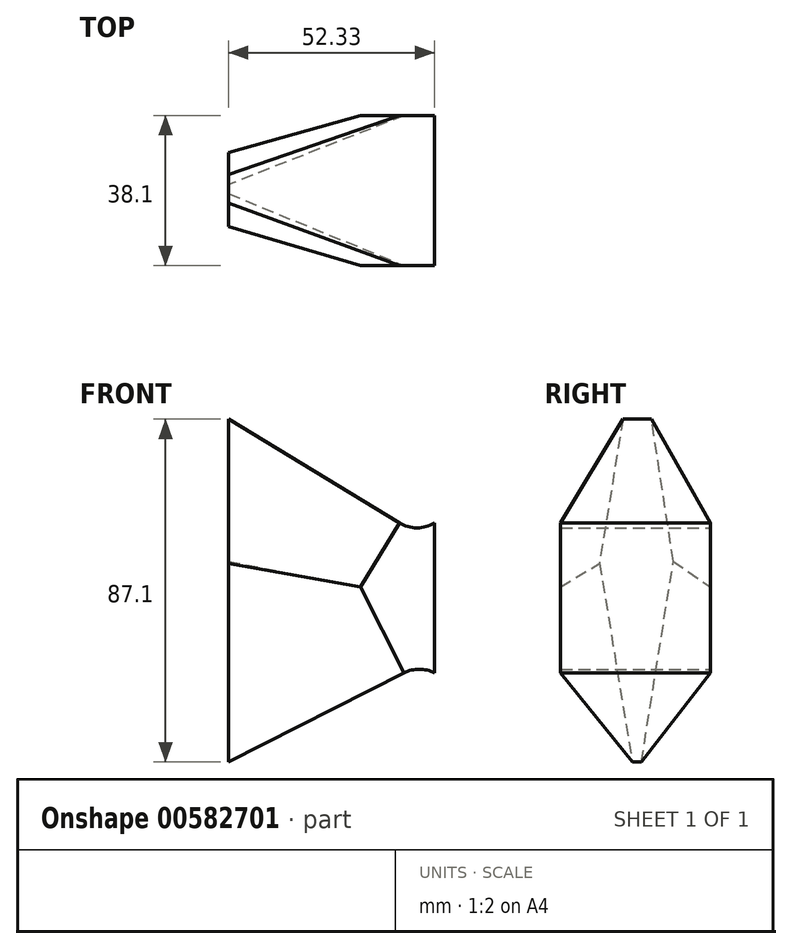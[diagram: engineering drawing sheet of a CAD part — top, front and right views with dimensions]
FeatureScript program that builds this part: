
annotation { "Feature Type Name" : "Feature", "Feature Type Description" : "" }
export const myFeature = defineFeature(function(context is Context, id is Id, definition is map)
    precondition{}
    {
        {
            var Q0;
            Q0=qCreatedBy(makeId("Front.planeOp"),FACE);
            var sketch = newSketch(context, id + "F0", { "sketchPlane" : qUnion([Q0])});
            skLineSegment(sketch, "E0", {"start": v(27.77, 20.35) * mm, "end": v(27.77, -17.75) * mm});
            skArc(sketch, "E1", {"start": v(18.86, 20.35) * mm, "mid": v(23.32, 19.1) * mm, "end": v(27.77, 20.35) * mm});
            skArc(sketch, "E2", {"start": v(27.77, -17.75) * mm, "mid": v(23.9, -16.83) * mm, "end": v(20, -17.75) * mm});
            skLineSegment(sketch, "E3", {"start": v(18.86, 20.35) * mm, "end": v(-24.56, 46.72) * mm});
            skLineSegment(sketch, "E4", {"start": v(20, -17.75) * mm, "end": v(-24.56, -40.38) * mm});
            skLineSegment(sketch, "E5", {"start": v(-24.56, -40.38) * mm, "end": v(-24.56, 46.72) * mm});
            skSolve(sketch);
        }
        {
            var Q0;
            Q0 = qSketchRegion(id + "F0", true);
            extrude(context, id + "F1", {"entities" : qUnion([Q0]), "depth" : 38.1 * mm, "offsetDistance" : 25.4 * mm});
        }
        {
            var Q0;
            Q0=makeQuery(id+"F1.opExtrude","SWEPT_FACE",FACE,{"disambiguationData":[OSD([sQuery(id+"F0.wireOp",EDGE,"E4")])]});
            var sketch = newSketch(context, id + "F2", { "sketchPlane" : qUnion([Q0])});
            skLineSegment(sketch, "E6.0", {"start": v(9.8, 0) * mm, "end": v(-40.17, 0) * mm});
            skLineSegment(sketch, "E7.0", {"start": v(-40.17, 38.1) * mm, "end": v(-40.17, 0) * mm});
            skLineSegment(sketch, "E8.0", {"start": v(9.8, 38.1) * mm, "end": v(-40.17, 38.1) * mm});
            skLineSegment(sketch, "E9", {"start": v(9.8, 0) * mm, "end": v(-40.17, 17.52) * mm});
            skLineSegment(sketch, "E10", {"start": v(-40.17, 19.86) * mm, "end": v(9.8, 38.1) * mm});
            skLineSegment(sketch, "E11.0", {"start": v(33.97, 38.1) * mm, "end": v(16.73, 38.1) * mm, "construction": true});
            skLineSegment(sketch, "E12.0", {"start": v(33.97, 38.1) * mm, "end": v(16.73, 38.1) * mm});
            skSolve(sketch);
        }
        {
            var Q0;
            {var subQ0=sQuery(id+"F2.wireOp",EDGE,"E6.0");Q0=makeQuery(id+"F2.imprint","IMPRINT",FACE,{"disambiguationData":[TD([[makeQuery(id+"F2.imprint","IMPRINT",EDGE,{"derivedFrom":subQ0}),-1.0]])]});}
            var Q1;
            {var subQ0=sQuery(id+"F2.wireOp",EDGE,"E8.0");Q1=makeQuery(id+"F2.imprint","IMPRINT",FACE,{"disambiguationData":[TD([[makeQuery(id+"F2.imprint","IMPRINT",EDGE,{"derivedFrom":subQ0}),1.0]])]});}
            extrude(context, id + "F3", {"entities" : qUnion([Q0, Q1]), "operationType" : NewBodyOperationType.REMOVE, "oppositeDirection" : true, "depth" : 101.6 * mm, "offsetDistance" : 25.4 * mm});
        }
        {
            var Q0;
            Q0=makeQuery(id+"F1.opExtrude","SWEPT_FACE",FACE,{"disambiguationData":[OSD([sQuery(id+"F0.wireOp",EDGE,"E3")])]});
            var sketch = newSketch(context, id + "F4", { "sketchPlane" : qUnion([Q0])});
            skLineSegment(sketch, "E13", {"start": v(5.55, -38.1) * mm, "end": v(-45.25, -22.26) * mm});
            skLineSegment(sketch, "E14", {"start": v(-45.25, -22.26) * mm, "end": v(-45.25, -14.97) * mm});
            skLineSegment(sketch, "E15", {"start": v(-45.25, -14.97) * mm, "end": v(5.55, 0) * mm});
            skSolve(sketch);
        }
        {
            var Q0;
            {var subQ0=sQuery(id+"F4.wireOp",EDGE,"E13");Q0=makeQuery(id+"F4.imprint","IMPRINT",FACE,{"disambiguationData":[TD([[makeQuery(id+"F4.imprint","IMPRINT",EDGE,{"derivedFrom":subQ0}),1.0]])]});}
            var Q1;
            {var subQ0=sQuery(id+"F4.wireOp",EDGE,"E15");Q1=makeQuery(id+"F4.imprint","IMPRINT",FACE,{"disambiguationData":[TD([[makeQuery(id+"F4.imprint","IMPRINT",EDGE,{"derivedFrom":subQ0}),1.0]])]});}
            extrude(context, id + "F5", {"entities" : qUnion([Q0, Q1]), "operationType" : NewBodyOperationType.REMOVE, "oppositeDirection" : true, "depth" : 127 * mm, "offsetDistance" : 25.4 * mm});
        }
    });
